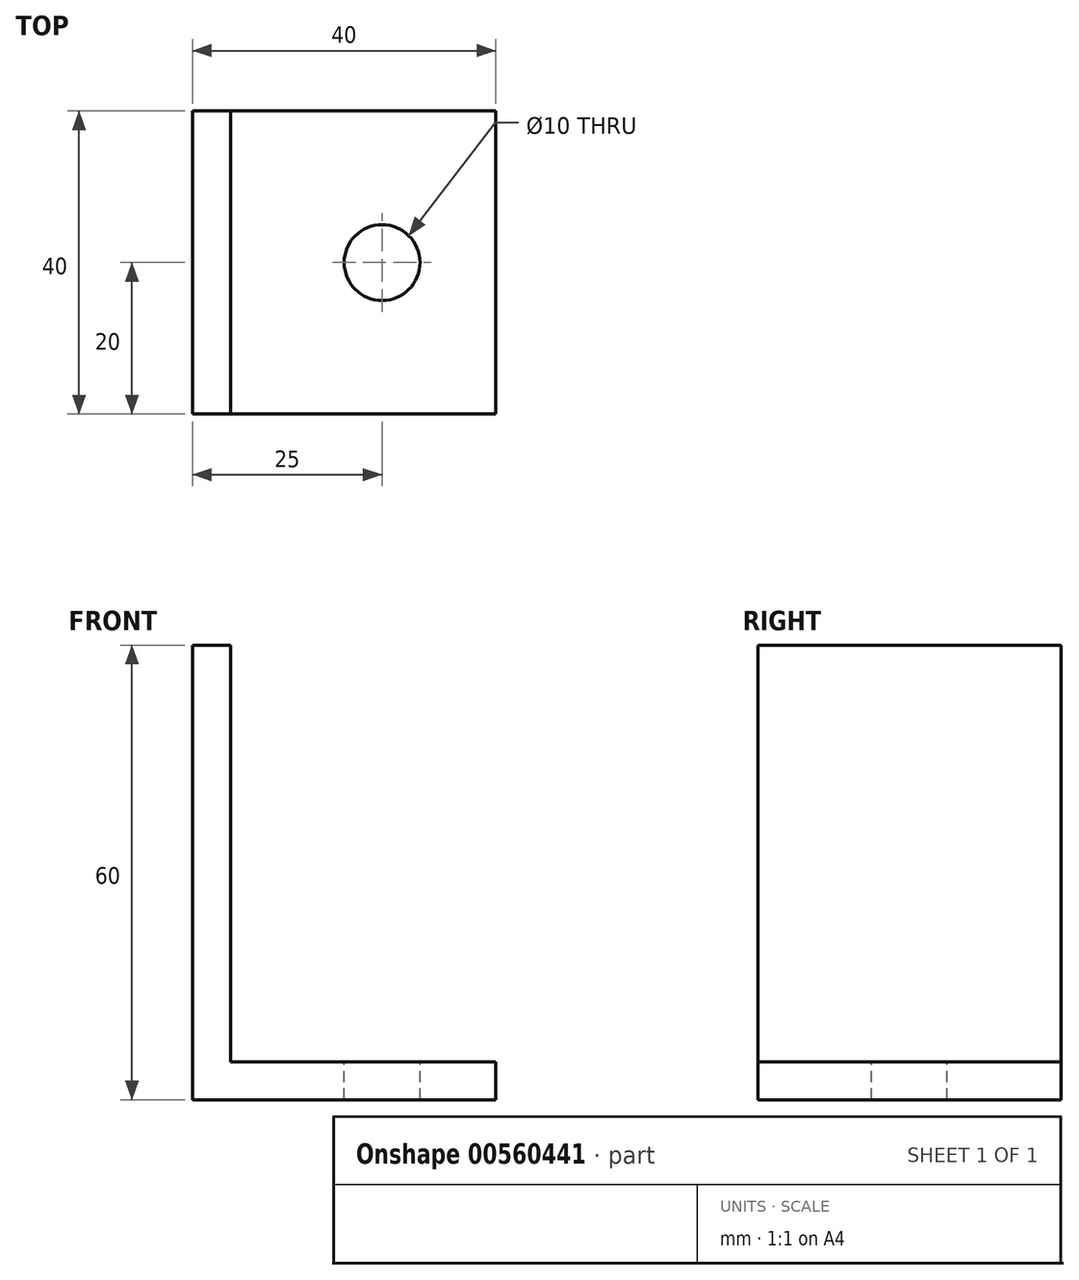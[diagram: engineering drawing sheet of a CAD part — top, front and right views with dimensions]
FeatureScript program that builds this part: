
annotation { "Feature Type Name" : "Feature", "Feature Type Description" : "" }
export const myFeature = defineFeature(function(context is Context, id is Id, definition is map)
    precondition{}
    {
        {
            var Q0;
            Q0=qCreatedBy(makeId("Front.planeOp"),FACE);
            var sketch = newSketch(context, id + "F0", { "sketchPlane" : qUnion([Q0])});
            skLineSegment(sketch, "E0", {"start": v(0, 0) * mm, "end": v(0, 60) * mm});
            skLineSegment(sketch, "E1", {"start": v(0, 0) * mm, "end": v(40, 0) * mm});
            skLineSegment(sketch, "E2.0", {"start": v(5, 5) * mm, "end": v(5, 60) * mm});
            skLineSegment(sketch, "E2.1", {"start": v(5, 5) * mm, "end": v(40, 5) * mm});
            skLineSegment(sketch, "E3", {"start": v(0, 60) * mm, "end": v(5, 60) * mm});
            skLineSegment(sketch, "E4", {"start": v(40, 5) * mm, "end": v(40, 0) * mm});
            skSolve(sketch);
        }
        {
            var Q0;
            Q0=makeQuery(id+"F0.imprint","IMPRINT",FACE,{"disambiguationData":[TD([[makeQuery(id+"F0.imprint","IMPRINT",EDGE,{"derivedFrom":sQuery(id+"F0.wireOp",EDGE,"E0")}),-1.0]])]});
            extrude(context, id + "F1", {"entities" : qUnion([Q0]), "endBound" : BoundingType.SYMMETRIC, "depth" : 40 * mm, "offsetDistance" : 25 * mm});
        }
        {
            var Q0;
            Q0=makeQuery(id+"F1.opExtrude","SWEPT_FACE",FACE,{"disambiguationData":[OSD([sQuery(id+"F0.wireOp",EDGE,"E2.1")])]});
            var sketch = newSketch(context, id + "F2", { "sketchPlane" : qUnion([Q0])});
            skCircle(sketch, "E5", {"center": v(25, 0) * mm, "radius": 5 * mm});
            skSolve(sketch);
        }
        {
            var Q0;
            Q0=sQuery(id+"F2.wireOp",VERTEX,"E5.center");
            var Q1;
            Q1=makeQuery(id+"F1.opExtrude","SWEPT_BODY",BODY,{"disambiguationData":[OSD([sQuery(id+"F0.wireOp",EDGE,"E0"),sQuery(id+"F0.wireOp",EDGE,"E1"),sQuery(id+"F0.wireOp",EDGE,"E2.0"),sQuery(id+"F0.wireOp",EDGE,"E2.1"),sQuery(id+"F0.wireOp",EDGE,"E3"),sQuery(id+"F0.wireOp",EDGE,"E4")])]});
            hole(context, id + "F3", {"style" : HoleStyle.SIMPLE, "endStyle" : HoleEndStyle.THROUGH, "holeDiameter" : 10 * mm, "isTappedThrough" : true, "tappedDepth" : 12 * mm, "tapClearance" : 3, "locations" : qUnion([Q0]), "scope" : qUnion([Q1])});
        }
    });
